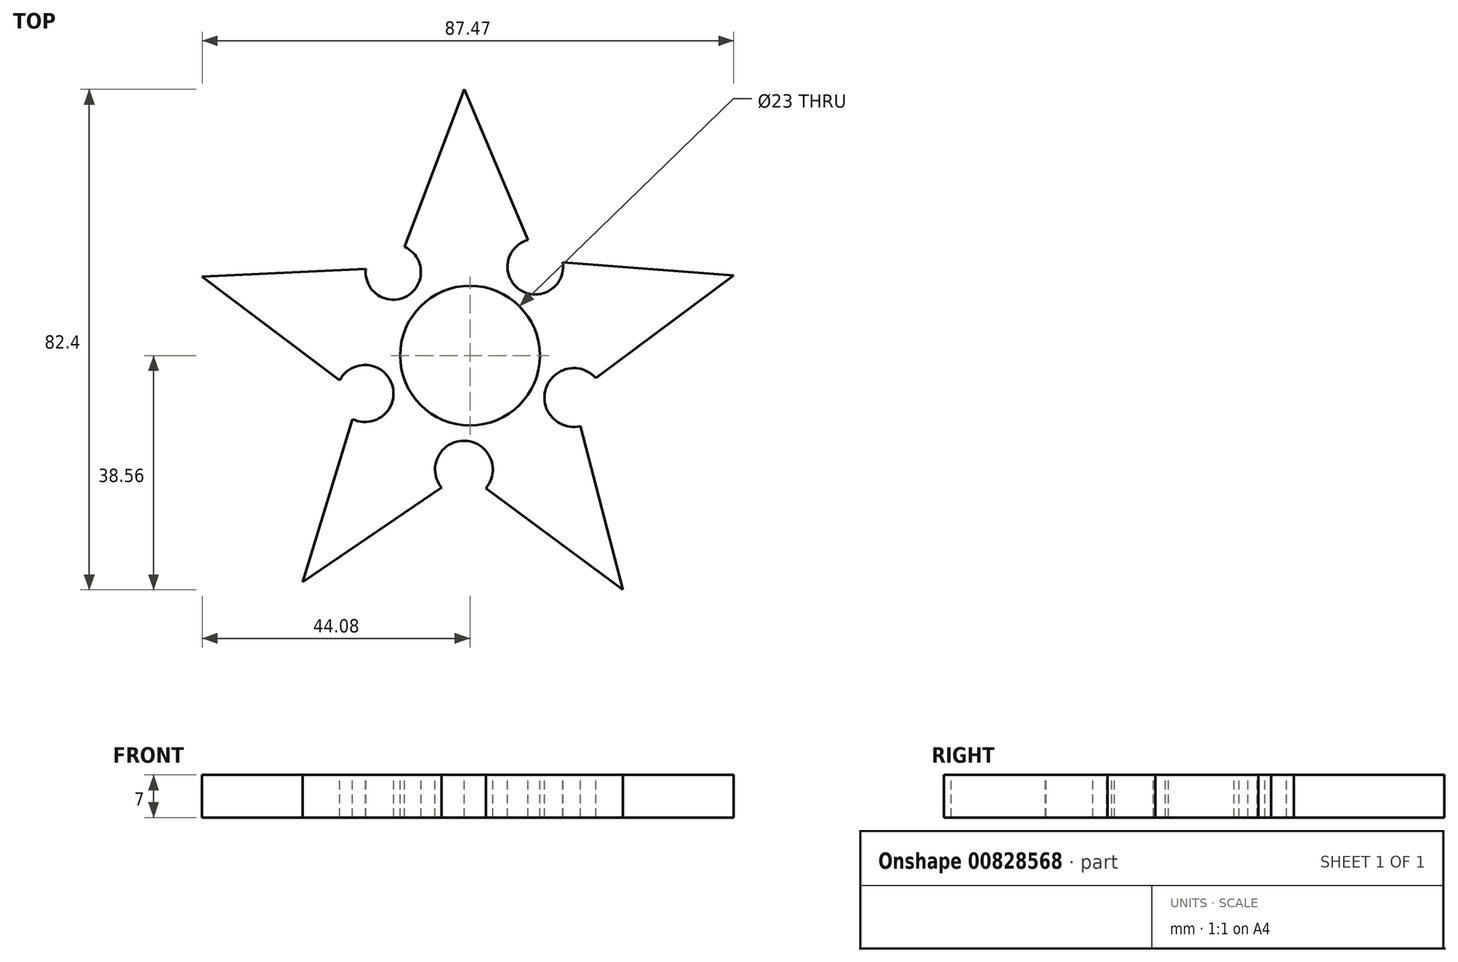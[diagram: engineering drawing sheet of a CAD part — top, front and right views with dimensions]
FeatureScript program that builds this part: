
annotation { "Feature Type Name" : "Feature", "Feature Type Description" : "" }
export const myFeature = defineFeature(function(context is Context, id is Id, definition is map)
    precondition{}
    {
        {
            var Q0;
            Q0=qCreatedBy(makeId("Top.planeOp"),FACE);
            var sketch = newSketch(context, id + "F0", { "sketchPlane" : qUnion([Q0])});
            skCircle(sketch, "E0", {"center": v(0, 0) * mm, "radius": 11 * mm});
            skSolve(sketch);
        }
        {
            var Q0;
            Q0=qCreatedBy(makeId("Top.planeOp"),FACE);
            var sketch = newSketch(context, id + "F1", { "sketchPlane" : qUnion([Q0])});
            skArc(sketch, "E1", {"start": v(-17.14, 14.29) * mm, "mid": v(-10.39, 9.78) * mm, "end": v(-10.75, 17.89) * mm});
            skArc(sketch, "E2", {"start": v(9.54, 19.05) * mm, "mid": v(8.26, 10.8) * mm, "end": v(15.26, 15.34) * mm});
            skArc(sketch, "E3", {"start": v(20.74, -3.72) * mm, "mid": v(12.49, -5.42) * mm, "end": v(18.18, -11.62) * mm});
            skArc(sketch, "E4", {"start": v(2.61, -21.84) * mm, "mid": v(-0.92, -14.02) * mm, "end": v(-4.7, -21.73) * mm});
            skArc(sketch, "E5", {"start": v(-19.34, -10.46) * mm, "mid": v(-12.82, -4.79) * mm, "end": v(-21.44, -4.07) * mm});
            skLineSegment(sketch, "E6", {"start": v(-10.75, 17.89) * mm, "end": v(-0.92, 43.84) * mm});
            skPoint(sketch, "E6.endSnap0", {"position": v(-0.92, -14.02) * mm});
            skLineSegment(sketch, "E7", {"start": v(-0.92, 43.84) * mm, "end": v(9.54, 19.05) * mm});
            skLineSegment(sketch, "E8", {"start": v(15.26, 15.34) * mm, "end": v(43.39, 13.2) * mm});
            skLineSegment(sketch, "E9", {"start": v(43.39, 13.2) * mm, "end": v(20.74, -3.72) * mm});
            skLineSegment(sketch, "E10", {"start": v(-4.7, -21.73) * mm, "end": v(-27.52, -37.32) * mm});
            skLineSegment(sketch, "E11", {"start": v(-27.52, -37.32) * mm, "end": v(-19.34, -10.46) * mm});
            skLineSegment(sketch, "E12", {"start": v(-21.44, -4.07) * mm, "end": v(-44.08, 13.02) * mm});
            skLineSegment(sketch, "E13", {"start": v(-44.08, 13.02) * mm, "end": v(-17.14, 14.29) * mm});
            skLineSegment(sketch, "E14", {"start": v(2.61, -21.84) * mm, "end": v(25.15, -38.56) * mm});
            skLineSegment(sketch, "E15", {"start": v(25.15, -38.56) * mm, "end": v(18.18, -11.62) * mm});
            skSolve(sketch);
        }
        {
            var Q0;
            Q0 = qSketchRegion(id + "F1", true);
            extrude(context, id + "F2", {"entities" : qUnion([Q0]), "oppositeDirection" : true, "depth" : 7 * mm, "offsetDistance" : 25.4 * mm});
        }
        {
            var Q0;
            Q0=makeQuery(id+"F0.imprint","IMPRINT",FACE,{"disambiguationData":[TD([[makeQuery(id+"F0.imprint","IMPRINT",EDGE,{"derivedFrom":sQuery(id+"F0.wireOp",EDGE,"E0")}),1.0]])]});
            var sketch = newSketch(context, id + "F3", { "sketchPlane" : qUnion([Q0])});
            skCircle(sketch, "E16", {"center": v(0, 0) * mm, "radius": 11.5 * mm});
            skSolve(sketch);
        }
        {
            var Q0;
            Q0 = qSketchRegion(id + "F3", true);
            extrude(context, id + "F4", {"entities" : qUnion([Q0]), "operationType" : NewBodyOperationType.REMOVE, "oppositeDirection" : true, "depth" : 25.4 * mm, "offsetDistance" : 25.4 * mm});
        }
    });
